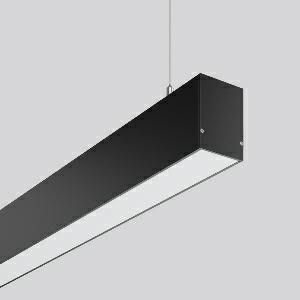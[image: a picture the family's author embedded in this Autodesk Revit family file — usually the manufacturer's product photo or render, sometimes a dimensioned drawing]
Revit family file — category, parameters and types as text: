
# Revit family: less_is_more_50_312319_003_1_f851
name_source: partatom
category: Lighting Fixtures
units: mm (PartAtom-declared; Revit-internal decimal feet)

## family parameters
Cut with Voids When Loaded = No
Host = Face
Light Source = No
Part Type = Normal
Room Calculation Point = No
Round Connector Dimension = Use Diameter
Shared = No

## types (1)
- LESS IS MORE 50 (1 x LED Modul 840, 6450 lm, 4000)
    Apparent Load = 52 VA
    CIE Flux Codes = 49 80 96 63 100
    Color Rendering = 80
    Color Temperature = 4000
    Default Elevation = 1800 mm
    Description = Series: LESS IS MORE 50
Linear pendant luminaire for aesthetically sophisticated lighting. Housing: extruded aluminium profile, powder-coated. End cap aluminium powder-coated. Canopy made of aluminium, powder-coated. Diffuser made of non-yellowing plastic (PMMA), opal. Direct 65%, indirect 35% light emission. Suitable for pendant. 2-point steel cable suspension freely positionable and infinitely height-adjustable. Special lengths available on request. LED unit with integrated converter interchangeable and removable. Suitable for through-wiring. With sensors or as a safety luminaire on request. 
Colour: deep black, matt (RAL 9005)
Length: 1407 mm
Width: 57 mm
Height: 75 mm
Suspension length: 2000 mm
Lamp: LED
Socket: without socket
Colour temperature: 4000K
Colour rendering index (CRI): 80
Light source: LED
Socket lamp2: Without base
Colour temperature: 4000K
System power: 52 W
Rated luminous flux: 6450 lm
Luminous efficiency: 124 lm/W
Control gear: Regulated power supply
Control gear: Regulated power supply
Protection class: I
Type of protection: IP 20
    Height = 75 mm
    Lamp = 1 x LED Modul 840
    Lamp Light Flux = 6450 lm
    Lamp count = 1
    Length = 1407 mm
    Lifetime = 50000 h
    Luminous efficacy = 124 lm/W
    Manufacturer = RZB
    ModVariant = No
    Model = 312319.003.1
    Mounting Place = Ceiling
    Mounting Type = Pendant
    Number of Poles = 1
    OnlyDefault = Yes
    Power Factor = 1
    Product Name = LESS IS MORE 50
    Product group = Pendant LED linear luminaires
    ProductGroupID = 907
    Protection Class = Protection class I
    Protection Degree = IP 20
    RLX_Detail_Level = 1
    RLX_Emergency_Light_Flux = 0 lm
    RLX_Emergency_Type = 0
    RLX_Emergency_Type_DB = No
    RlxData = <blob elided: 39885 chars, md5=9beb80db>
    Socket = socket
    Standby Power = 0 W
    System Light Flux = 6450 lm
    System Power = 52 W
    Type Comments = Product without accessories
    Type Image = 312318.003.jpg
    URL = http://relux.com
    VarID = ---
    Voltage = 230 V
    Voltage Range = 220-240 V
    Weight = 0.00 kg
    Width = 57 mm

## geometry (parser evidence)
native form markers: Blend x4, Sweep x14
no freeform markers — native parametric forms only
